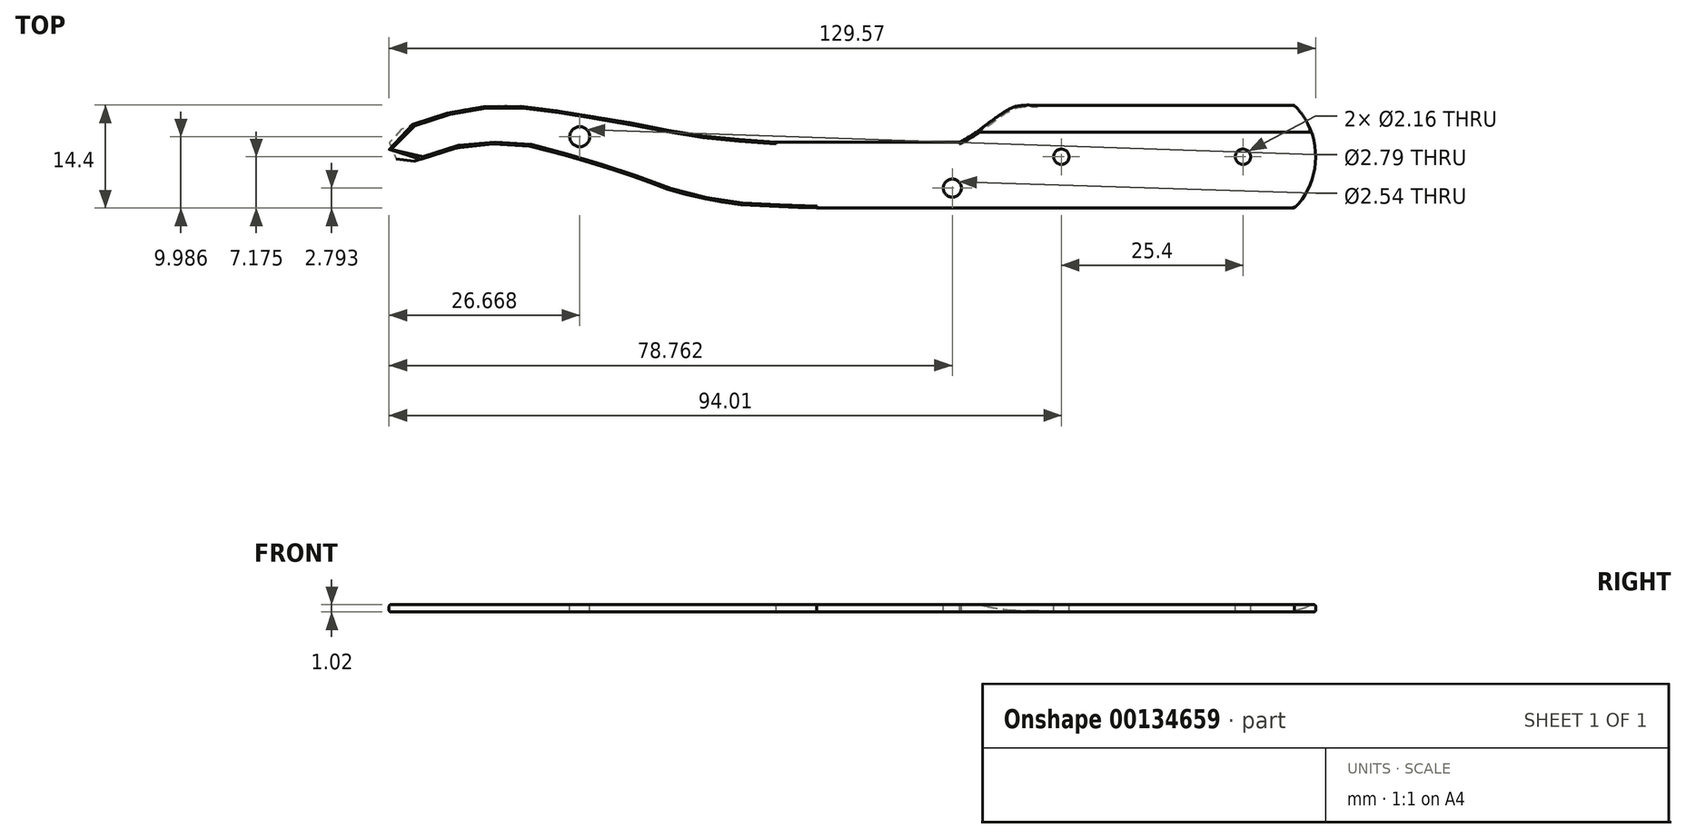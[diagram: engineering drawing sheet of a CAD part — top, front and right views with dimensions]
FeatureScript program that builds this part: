
annotation { "Feature Type Name" : "Feature", "Feature Type Description" : "" }
export const myFeature = defineFeature(function(context is Context, id is Id, definition is map)
    precondition{}
    {
        {
            var Q0;
            Q0=qCreatedBy(makeId("Top.planeOp"),FACE);
            var sketch = newSketch(context, id + "F0", { "sketchPlane" : qUnion([Q0])});
            skPoint(sketch, "E0", {"position": v(130.8, 0) * mm});
            skPoint(sketch, "E1", {"position": v(-103.94, -143.52) * mm});
            skPoint(sketch, "E2", {"position": v(0.55, 0.24) * mm});
            skPoint(sketch, "E3", {"position": v(0.4, 1.22) * mm});
            skPoint(sketch, "E4", {"position": v(0.7, 2.2) * mm});
            skPoint(sketch, "E5", {"position": v(1.36, 2.96) * mm});
            skPoint(sketch, "E6", {"position": v(5, 4.63) * mm});
            skPoint(sketch, "E7", {"position": v(9.58, 5.96) * mm});
            skPoint(sketch, "E8", {"position": v(14.71, 6.72) * mm});
            skPoint(sketch, "E9", {"position": v(19.41, 6.61) * mm});
            skPoint(sketch, "E10", {"position": v(22.67, 6.26) * mm});
            skPoint(sketch, "E11", {"position": v(23.56, 6.1) * mm});
            skPoint(sketch, "E12", {"position": v(33.06, 4.54) * mm});
            skPoint(sketch, "E13", {"position": v(37.97, 3.6) * mm});
            skPoint(sketch, "E14", {"position": v(42.95, 2.72) * mm});
            skPoint(sketch, "E15", {"position": v(46.9, 2.26) * mm});
            skPoint(sketch, "E16", {"position": v(51.6, 1.8) * mm});
            skPoint(sketch, "E17", {"position": v(54.47, 1.63) * mm});
            skPoint(sketch, "E18", {"position": v(80.16, 1.63) * mm});
            skPoint(sketch, "E19", {"position": v(82.68, 3.16) * mm});
            skPoint(sketch, "E20", {"position": v(83.83, 4.04) * mm});
            skPoint(sketch, "E21", {"position": v(85.06, 4.93) * mm});
            skPoint(sketch, "E22", {"position": v(86.43, 5.87) * mm});
            skPoint(sketch, "E23", {"position": v(87.8, 6.58) * mm});
            skPoint(sketch, "E24", {"position": v(89.43, 6.85) * mm});
            skPoint(sketch, "E25", {"position": v(91.29, 6.78) * mm});
            skPoint(sketch, "E26", {"position": v(127.01, 6.78) * mm});
            skPoint(sketch, "E27", {"position": v(128.33, 5.87) * mm});
            skPoint(sketch, "E28", {"position": v(129.3, 4.49) * mm});
            skPoint(sketch, "E29", {"position": v(130.18, 1.72) * mm});
            skPoint(sketch, "E30", {"position": v(130.35, -0.84) * mm});
            skPoint(sketch, "E31", {"position": v(129.95, -2.76) * mm});
            skPoint(sketch, "E32", {"position": v(128.97, -5.52) * mm});
            skPoint(sketch, "E33", {"position": v(127.42, -7.1) * mm});
            skPoint(sketch, "E34", {"position": v(127.01, -7.57) * mm});
            skPoint(sketch, "E35", {"position": v(60.22, -7.57) * mm});
            skPoint(sketch, "E36", {"position": v(53.63, -7.32) * mm});
            skPoint(sketch, "E37", {"position": v(47.48, -6.84) * mm});
            skPoint(sketch, "E38", {"position": v(41.94, -5.64) * mm});
            skPoint(sketch, "E39", {"position": v(38.32, -4.6) * mm});
            skPoint(sketch, "E40", {"position": v(34.93, -3.26) * mm});
            skPoint(sketch, "E41", {"position": v(22.9, 0.41) * mm});
            skPoint(sketch, "E42", {"position": v(19.37, 1.23) * mm});
            skPoint(sketch, "E43", {"position": v(15.74, 1.42) * mm});
            skPoint(sketch, "E44", {"position": v(11.4, 1.13) * mm});
            skPoint(sketch, "E45", {"position": v(8.54, 0.52) * mm});
            skPoint(sketch, "E46", {"position": v(5.77, 0) * mm});
            skPoint(sketch, "E47", {"position": v(4.05, -0.96) * mm});
            skPoint(sketch, "E48", {"position": v(2.62, -1.15) * mm});
            skPoint(sketch, "E49", {"position": v(1.82, -0.96) * mm});
            skPoint(sketch, "E50", {"position": v(1.25, -0.57) * mm});
            skPoint(sketch, "E51", {"position": v(0.81, -0.18) * mm});
            skLineSegment(sketch, "E52", {"start": v(91.29, 6.78) * mm, "end": v(127.01, 6.78) * mm});
            skLineSegment(sketch, "E53", {"start": v(60.22, -7.57) * mm, "end": v(127.01, -7.57) * mm});
            skLineSegment(sketch, "E54", {"start": v(54.47, 1.63) * mm, "end": v(80.16, 1.63) * mm});
            skFitSpline(sketch, "E55", {"points": [v(80.16, 1.63) * mm, v(82.68, 3.16) * mm, v(83.83, 4.04) * mm, v(85.06, 4.93) * mm, v(86.43, 5.87) * mm, v(87.8, 6.58) * mm, v(89.43, 6.85) * mm, v(91.29, 6.78) * mm], "startDerivative": vector(15.23, 8.8) * mm, "endDerivative": vector(12.83, -0.9) * mm});
            skArc(sketch, "E56", {"start": v(127.01, -7.57) * mm, "mid": v(129.97, -0.4) * mm, "end": v(127.01, 6.78) * mm});
            skFitSpline(sketch, "E57", {"points": [v(60.22, -7.57) * mm, v(53.63, -7.32) * mm, v(47.48, -6.84) * mm, v(41.94, -5.64) * mm, v(38.32, -4.6) * mm, v(34.93, -3.26) * mm, v(22.9, 0.41) * mm, v(19.37, 1.23) * mm, v(15.74, 1.42) * mm, v(11.4, 1.13) * mm, v(8.54, 0.52) * mm, v(4.05, -0.96) * mm, v(2.62, -1.15) * mm, v(1.82, -0.96) * mm, v(1.25, -0.57) * mm, v(0.81, -0.18) * mm, v(0.55, 0.24) * mm, v(0.4, 1.22) * mm, v(0.7, 2.2) * mm, v(1.36, 2.96) * mm, v(5, 4.63) * mm, v(9.58, 5.96) * mm, v(14.71, 6.72) * mm, v(19.41, 6.61) * mm, v(22.67, 6.26) * mm, v(23.56, 6.1) * mm, v(33.06, 4.54) * mm, v(37.97, 3.6) * mm, v(42.95, 2.72) * mm, v(46.9, 2.26) * mm, v(51.6, 1.8) * mm, v(54.47, 1.63) * mm], "startDerivative": vector(-147, 5.5) * mm, "endDerivative": vector(89.1, -4.43) * mm});
            skSolve(sketch);
        }
        {
            var Q0;
            Q0=qSketchRegion(id+"F0",true);
            extrude(context, id + "F1", {"entities" : qUnion([Q0]), "depth" : 1.02 * mm});
        }
        {
            var Q0;
            Q0=makeQuery(id+"F1.opExtrude","CAP_FACE",FACE,{"disambiguationData":[OSD([sQuery(id+"F0.wireOp",EDGE,"E52"),sQuery(id+"F0.wireOp",EDGE,"E53"),sQuery(id+"F0.wireOp",EDGE,"E54"),sQuery(id+"F0.wireOp",EDGE,"E55"),sQuery(id+"F0.wireOp",EDGE,"E56"),sQuery(id+"F0.wireOp",EDGE,"E57")])],"isStart":false});
            var sketch = newSketch(context, id + "F2", { "sketchPlane" : qUnion([Q0])});
            skCircle(sketch, "E58", {"center": v(119.81, -0.4) * mm, "radius": 1.08 * mm});
            skPoint(sketch, "E58.centerSnap0", {"position": v(129.97, -0.4) * mm});
            skCircle(sketch, "E59", {"center": v(94.41, -0.4) * mm, "radius": 1.08 * mm});
            skSolve(sketch);
        }
        {
            var Q0;
            Q0=makeQuery(id+"F2.imprint","IMPRINT",FACE,{"disambiguationData":[TD([[makeQuery(id+"F2.imprint","IMPRINT",EDGE,{"derivedFrom":sQuery(id+"F2.wireOp",EDGE,"E58")}),-1.0]])]});
            var sketch = newSketch(context, id + "F3", { "sketchPlane" : qUnion([Q0])});
            skCircle(sketch, "E60", {"center": v(27.07, 2.42) * mm, "radius": 1.4 * mm});
            skPoint(sketch, "E61", {"position": v(0.4, 1.03) * mm});
            skSolve(sketch);
        }
        {
            var Q0;
            Q0=qSketchRegion(id+"F3",true);
            extrude(context, id + "F4", {"entities" : qUnion([Q0]), "operationType" : NewBodyOperationType.REMOVE, "endBound" : BoundingType.THROUGH_ALL, "oppositeDirection" : true, "depth" : 25.4 * mm});
        }
        {
            var Q0;
            Q0 = qSketchRegion(id + "F2", true);
            extrude(context, id + "F5", {"entities" : qUnion([Q0]), "operationType" : NewBodyOperationType.REMOVE, "endBound" : BoundingType.THROUGH_ALL, "oppositeDirection" : true, "depth" : 25.4 * mm});
        }
        {
            var Q0;
            Q0=qCreatedBy(makeId("Right.planeOp"),FACE);
            cPlane(context, id + "F6", {"entities" : qUnion([Q0]), "cplaneType" : CPlaneType.OFFSET, "offset" : 152.4 * mm, "width" : 152.4 * mm, "height" : 152.4 * mm});
        }
        {
            var Q0;
            Q0=qCreatedBy(id+"F6.planeOp",FACE);
            var sketch = newSketch(context, id + "F7", { "sketchPlane" : qUnion([Q0])});
            skLineSegment(sketch, "E62", {"start": v(6.86, 1.02) * mm, "end": v(6.86, 0.14) * mm});
            skLineSegment(sketch, "E63", {"start": v(6.86, 0.14) * mm, "end": v(3.05, 1.02) * mm});
            skLineSegment(sketch, "E64", {"start": v(3.05, 1.02) * mm, "end": v(6.86, 1.02) * mm});
            skSolve(sketch);
        }
        {
            var Q0;
            Q0 = qSketchRegion(id + "F7", true);
            extrude(context, id + "F8", {"entities" : qUnion([Q0]), "operationType" : NewBodyOperationType.REMOVE, "oppositeDirection" : true, "depth" : 73.66 * mm});
        }
        {
            var Q0;
            Q0=makeQuery(id+"F1.opExtrude","CAP_FACE",FACE,{"disambiguationData":[OSD([sQuery(id+"F0.wireOp",EDGE,"E52"),sQuery(id+"F0.wireOp",EDGE,"E53"),sQuery(id+"F0.wireOp",EDGE,"E54"),sQuery(id+"F0.wireOp",EDGE,"E55"),sQuery(id+"F0.wireOp",EDGE,"E56"),sQuery(id+"F0.wireOp",EDGE,"E57")])],"isStart":false});
            var sketch = newSketch(context, id + "F9", { "sketchPlane" : qUnion([Q0])});
            skCircle(sketch, "E65", {"center": v(79.16, -4.78) * mm, "radius": 1.27 * mm});
            skPoint(sketch, "E66", {"position": v(129.96, 0) * mm});
            skSolve(sketch);
        }
        {
            var Q0;
            Q0 = qSketchRegion(id + "F9", true);
            extrude(context, id + "F10", {"entities" : qUnion([Q0]), "operationType" : NewBodyOperationType.REMOVE, "endBound" : BoundingType.THROUGH_ALL, "oppositeDirection" : true, "depth" : 25.4 * mm});
        }
        {
            var Q0;
            Q0=makeQuery(id+"F1.opExtrude","CAP_EDGE",EDGE,{"disambiguationData":[OSD([sQuery(id+"F0.wireOp",EDGE,"E57")])],"isStart":false});
            var Q1;
            Q1=makeQuery(id+"F1.opExtrude","CAP_EDGE",EDGE,{"disambiguationData":[OSD([sQuery(id+"F0.wireOp",EDGE,"E53")])],"isStart":false});
            var Q2;
            Q2=makeQuery(id+"F1.opExtrude","CAP_EDGE",EDGE,{"disambiguationData":[OSD([sQuery(id+"F0.wireOp",EDGE,"E56")])],"isStart":false});
            var Q3;
            Q3=makeQuery(id+"F1.opExtrude","CAP_EDGE",EDGE,{"disambiguationData":[OSD([sQuery(id+"F0.wireOp",EDGE,"E54")])],"isStart":false});
            var Q4;
            Q4=makeQuery(id+"F1.opExtrude","CAP_EDGE",EDGE,{"disambiguationData":[OSD([sQuery(id+"F0.wireOp",EDGE,"E55")])],"isStart":false});
            var Q5;
            Q5=makeQuery(id+"F1.opExtrude","CAP_EDGE",EDGE,{"disambiguationData":[OSD([sQuery(id+"F0.wireOp",EDGE,"E53")])],"isStart":true});
            var Q6;
            Q6=makeQuery(id+"F1.opExtrude","CAP_EDGE",EDGE,{"disambiguationData":[OSD([sQuery(id+"F0.wireOp",EDGE,"E57")])],"isStart":true});
            var Q7;
            Q7=makeQuery(id+"F1.opExtrude","CAP_EDGE",EDGE,{"disambiguationData":[OSD([sQuery(id+"F0.wireOp",EDGE,"E54")])],"isStart":true});
            var Q8;
            Q8=makeQuery(id+"F1.opExtrude","CAP_EDGE",EDGE,{"disambiguationData":[OSD([sQuery(id+"F0.wireOp",EDGE,"E55")])],"isStart":true});
            var Q9;
            Q9=makeQuery(id+"F1.opExtrude","CAP_EDGE",EDGE,{"disambiguationData":[OSD([sQuery(id+"F0.wireOp",EDGE,"E52")])],"isStart":true});
            var Q10;
            Q10=makeQuery(id+"F1.opExtrude","CAP_EDGE",EDGE,{"disambiguationData":[OSD([sQuery(id+"F0.wireOp",EDGE,"E56")])],"isStart":true});
            var Q11;
            Q11=makeQuery(id+"F5.boolean.opBoolean","COPY",FACE,{"derivedFrom":makeQuery(id+"F5.opExtrude","SWEPT_FACE",FACE,{"disambiguationData":[OSD([sQuery(id+"F2.wireOp",EDGE,"E59")])]})});
            var Q12;
            Q12=makeQuery(id+"F5.boolean.opBoolean","COPY",FACE,{"derivedFrom":makeQuery(id+"F5.opExtrude","SWEPT_FACE",FACE,{"disambiguationData":[OSD([sQuery(id+"F2.wireOp",EDGE,"E58")])]})});
            fillet(context, id + "F11", {"entities" : qUnion([Q0, Q1, Q2, Q3, Q4, Q5, Q6, Q7, Q8, Q9, Q10, Q11, Q12]), "radius" : 0.25 * mm, "tangentPropagation" : true, "allowEdgeOverflow" : false});
        }
    });
